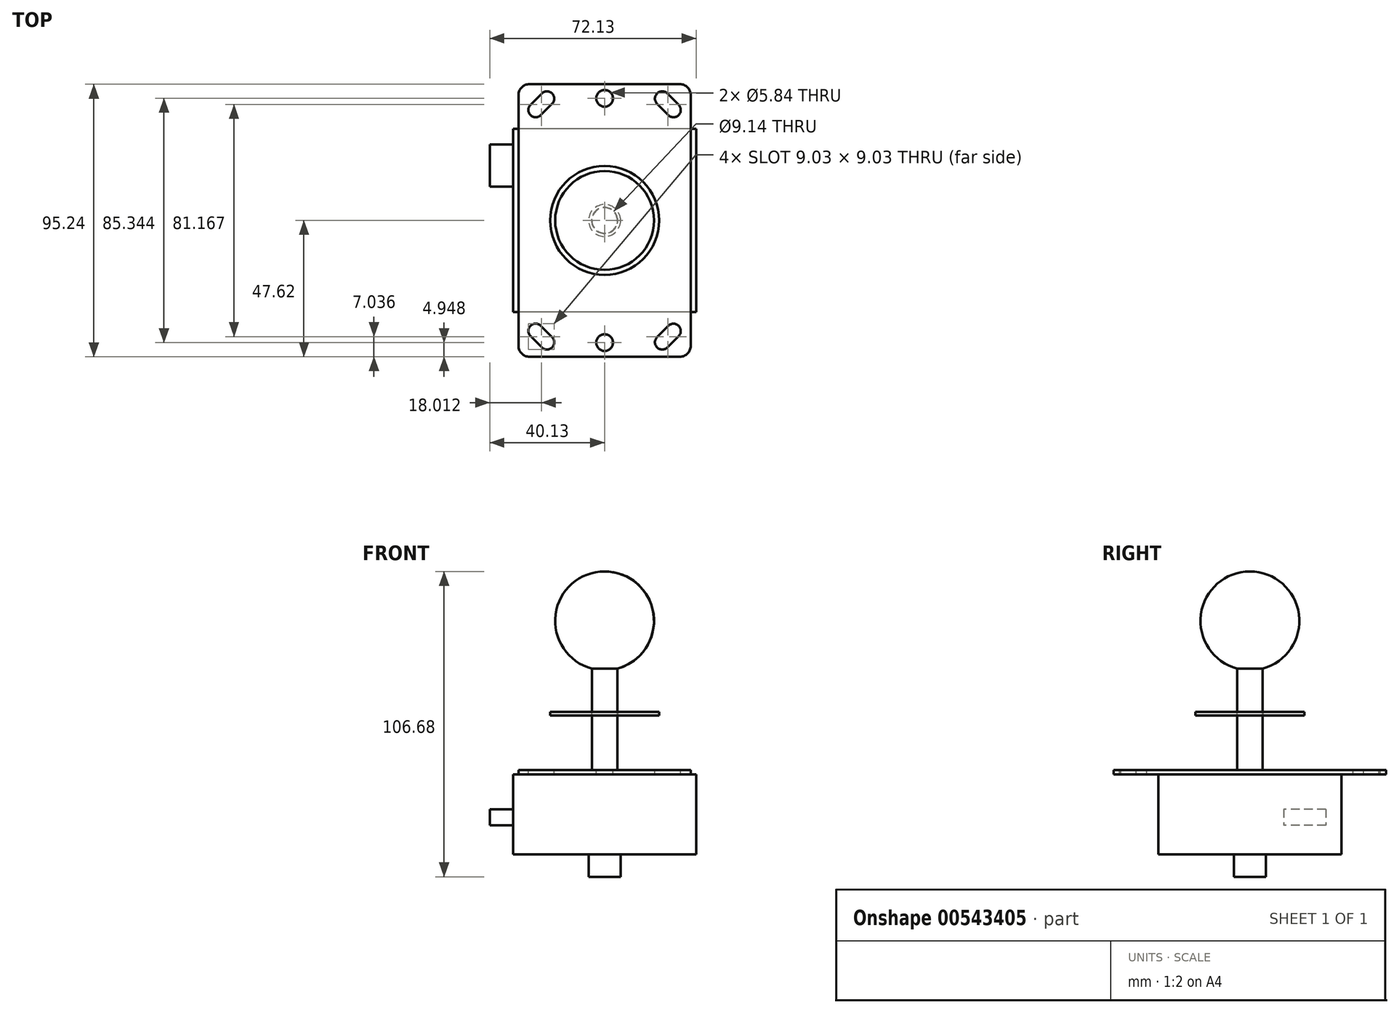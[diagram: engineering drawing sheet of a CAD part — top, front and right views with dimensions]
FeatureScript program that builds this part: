
annotation { "Feature Type Name" : "Feature", "Feature Type Description" : "" }
export const myFeature = defineFeature(function(context is Context, id is Id, definition is map)
    precondition{}
    {
        {
            var Q0;
            Q0=qCreatedBy(makeId("Top.planeOp"),FACE);
            var sketch = newSketch(context, id + "F0", { "sketchPlane" : qUnion([Q0])});
            skLineSegment(sketch, "E0.bottom", {"start": v(-30.1, 47.62) * mm, "end": v(30.1, 47.62) * mm});
            skLineSegment(sketch, "E0.top", {"start": v(-30.1, -47.63) * mm, "end": v(30.1, -47.63) * mm});
            skLineSegment(sketch, "E0.left", {"start": v(-30.1, 47.63) * mm, "end": v(-30.1, -47.63) * mm});
            skLineSegment(sketch, "E0.right", {"start": v(30.1, 47.63) * mm, "end": v(30.1, -47.63) * mm});
            skPoint(sketch, "E0.middle", {"position": v(0, 0) * mm});
            skSolve(sketch);
        }
        {
            var Q0;
            Q0 = qSketchRegion(id + "F0", true);
            extrude(context, id + "F1", {"entities" : qUnion([Q0]), "oppositeDirection" : true, "depth" : 1.52 * mm, "offsetDistance" : 25.4 * mm});
        }
        {
            var Q0;
            Q0=makeQuery(id+"F1.opExtrude","CAP_FACE",FACE,{"disambiguationData":[OSD([sQuery(id+"F0.wireOp",EDGE,"E0.bottom"),sQuery(id+"F0.wireOp",EDGE,"E0.top"),sQuery(id+"F0.wireOp",EDGE,"E0.left"),sQuery(id+"F0.wireOp",EDGE,"E0.right")])],"isStart":false});
            var sketch = newSketch(context, id + "F2", { "sketchPlane" : qUnion([Q0])});
            skLineSegment(sketch, "E1.bottom", {"start": v(32, 32) * mm, "end": v(-32, 32) * mm});
            skLineSegment(sketch, "E1.top", {"start": v(32, -32) * mm, "end": v(-32, -32) * mm});
            skLineSegment(sketch, "E1.left", {"start": v(32, 32) * mm, "end": v(32, -32) * mm});
            skLineSegment(sketch, "E1.right", {"start": v(-32, 32) * mm, "end": v(-32, -32) * mm});
            skPoint(sketch, "E1.middle", {"position": v(0, 0) * mm});
            skSolve(sketch);
        }
        {
            var Q0;
            Q0 = qSketchRegion(id + "F2", true);
            extrude(context, id + "F3", {"entities" : qUnion([Q0]), "operationType" : NewBodyOperationType.ADD, "depth" : 27.94 * mm, "offsetDistance" : 25.4 * mm});
        }
        {
            var Q0;
            {var subQ0=sQuery(id+"F0.wireOp",EDGE,"E0.right");var subQ1=sQuery(id+"F0.wireOp",EDGE,"E0.left");var subQ3=sQuery(id+"F0.wireOp",EDGE,"E0.top");Q0=makeQuery(id+"F3.boolean.opBoolean","SPLIT",FACE,{"disambiguationData":[TD([makeQuery(id+"F1.opExtrude","SWEPT_FACE",FACE,{"disambiguationData":[OSD([subQ3])]})])],"derivedFrom":makeQuery(id+"F1.opExtrude","CAP_FACE",FACE,{"disambiguationData":[OSD([sQuery(id+"F0.wireOp",EDGE,"E0.bottom"),subQ3,subQ1,subQ0])],"isStart":false})});}
            var sketch = newSketch(context, id + "F4", { "sketchPlane" : qUnion([Q0])});
            skCircle(sketch, "E2", {"center": v(0, 0) * mm, "radius": 5.59 * mm});
            skSolve(sketch);
        }
        {
            var Q0;
            Q0 = qSketchRegion(id + "F4", true);
            extrude(context, id + "F5", {"entities" : qUnion([Q0]), "operationType" : NewBodyOperationType.ADD, "depth" : 35.81 * mm, "offsetDistance" : 25.4 * mm});
        }
        {
            var Q0;
            Q0=qCreatedBy(makeId("Front.planeOp"),FACE);
            var sketch = newSketch(context, id + "F6", { "sketchPlane" : qUnion([Q0])});
            skArc(sketch, "E3", {"start": v(0, 69.34) * mm, "mid": v(-17.13, 54.31) * mm, "end": v(-4.45, 35.38) * mm});
            skLineSegment(sketch, "E4", {"start": v(-4.45, 35.38) * mm, "end": v(-4.44, 0) * mm});
            skLineSegment(sketch, "E5", {"start": v(-4.44, 0) * mm, "end": v(0, 0) * mm});
            skLineSegment(sketch, "E6", {"start": v(0, 0) * mm, "end": v(0, 69.34) * mm, "construction": true});
            skArc(sketch, "E7", {"start": v(-4.44, 35.38) * mm, "mid": v(-2.24, 34.94) * mm, "end": v(0, 34.8) * mm, "construction": true});
            skLineSegment(sketch, "E8", {"start": v(0, 69.34) * mm, "end": v(0, 0) * mm});
            skSolve(sketch);
        }
        {
            var Q0;
            Q0 = qSketchRegion(id + "F6", true);
            var Q1;
            Q1=sQuery(id+"F6.wireOp",EDGE,"E8");
            revolve(context, id + "F7", {"operationType" : NewBodyOperationType.ADD, "entities" : qUnion([Q0]), "axis" : qUnion([Q1]), "revolveType" : RevolveType.FULL});
        }
        {
            var Q0;
            Q0=makeQuery(id+"F1.opExtrude","CAP_FACE",FACE,{"disambiguationData":[OSD([sQuery(id+"F0.wireOp",EDGE,"E0.bottom"),sQuery(id+"F0.wireOp",EDGE,"E0.top"),sQuery(id+"F0.wireOp",EDGE,"E0.left"),sQuery(id+"F0.wireOp",EDGE,"E0.right")])],"isStart":true});
            var sketch = newSketch(context, id + "F8", { "sketchPlane" : qUnion([Q0])});
            skLineSegment(sketch, "E9", {"start": v(24.1, -38.6) * mm, "end": v(20.14, -42.56) * mm, "construction": true});
            skArc(sketch, "E10.0.startCap", {"start": v(22.3, -36.81) * mm, "mid": v(25.89, -36.81) * mm, "end": v(25.89, -40.4) * mm});
            skArc(sketch, "E10.0.endCap", {"start": v(21.94, -44.36) * mm, "mid": v(18.35, -44.36) * mm, "end": v(18.35, -40.76) * mm});
            skLineSegment(sketch, "E10.0.left", {"start": v(25.89, -40.4) * mm, "end": v(21.94, -44.36) * mm});
            skLineSegment(sketch, "E10.0.right", {"start": v(22.3, -36.81) * mm, "end": v(18.35, -40.76) * mm});
            skArc(sketch, "E11.0.startCap", {"start": v(22.3, -36.81) * mm, "mid": v(25.89, -36.81) * mm, "end": v(25.89, -40.4) * mm, "construction": true});
            skArc(sketch, "E11.0.endCap", {"start": v(21.94, -44.36) * mm, "mid": v(18.35, -44.36) * mm, "end": v(18.35, -40.76) * mm, "construction": true});
            skLineSegment(sketch, "E11.0.left", {"start": v(25.89, -40.4) * mm, "end": v(21.94, -44.36) * mm, "construction": true});
            skLineSegment(sketch, "E11.0.right", {"start": v(22.3, -36.81) * mm, "end": v(18.35, -40.76) * mm, "construction": true});
            skLineSegment(sketch, "E12.MirrorCS", {"start": v(-22.3, -36.81) * mm, "end": v(-18.35, -40.76) * mm});
            skLineSegment(sketch, "E13.MirrorCS", {"start": v(-25.89, -40.4) * mm, "end": v(-21.94, -44.36) * mm});
            skArc(sketch, "E14.MirrorCS", {"start": v(-22.3, -36.81) * mm, "mid": v(-25.89, -36.81) * mm, "end": v(-25.89, -40.4) * mm});
            skArc(sketch, "E15.MirrorCS", {"start": v(-21.94, -44.36) * mm, "mid": v(-18.35, -44.36) * mm, "end": v(-18.35, -40.76) * mm});
            skLineSegment(sketch, "E16.MirrorCS", {"start": v(-25.89, -40.4) * mm, "end": v(-21.94, -44.36) * mm, "construction": true});
            skArc(sketch, "E17.MirrorCS", {"start": v(-22.3, -36.81) * mm, "mid": v(-25.89, -36.81) * mm, "end": v(-25.89, -40.4) * mm, "construction": true});
            skLineSegment(sketch, "E18.MirrorCS", {"start": v(-24.1, -38.6) * mm, "end": v(-20.14, -42.56) * mm, "construction": true});
            skLineSegment(sketch, "E19.MirrorCS", {"start": v(-22.3, -36.81) * mm, "end": v(-18.35, -40.76) * mm, "construction": true});
            skArc(sketch, "E20.MirrorCS", {"start": v(-21.94, -44.36) * mm, "mid": v(-18.35, -44.36) * mm, "end": v(-18.35, -40.76) * mm, "construction": true});
            skArc(sketch, "E21.MirrorCS", {"start": v(-21.94, 44.36) * mm, "mid": v(-18.35, 44.36) * mm, "end": v(-18.35, 40.76) * mm});
            skLineSegment(sketch, "E22.MirrorCS", {"start": v(-22.3, 36.81) * mm, "end": v(-18.35, 40.76) * mm});
            skLineSegment(sketch, "E23.MirrorCS", {"start": v(-25.89, 40.4) * mm, "end": v(-21.94, 44.36) * mm});
            skArc(sketch, "E24.MirrorCS", {"start": v(-22.3, 36.81) * mm, "mid": v(-25.89, 36.81) * mm, "end": v(-25.89, 40.4) * mm});
            skArc(sketch, "E25.MirrorCS", {"start": v(21.94, 44.36) * mm, "mid": v(18.35, 44.36) * mm, "end": v(18.35, 40.76) * mm});
            skLineSegment(sketch, "E26.MirrorCS", {"start": v(-25.89, 40.4) * mm, "end": v(-21.94, 44.36) * mm, "construction": true});
            skArc(sketch, "E27.MirrorCS", {"start": v(22.3, 36.81) * mm, "mid": v(25.89, 36.81) * mm, "end": v(25.89, 40.4) * mm});
            skLineSegment(sketch, "E28.MirrorCS", {"start": v(-22.3, 36.81) * mm, "end": v(-18.35, 40.76) * mm, "construction": true});
            skLineSegment(sketch, "E29.MirrorCS", {"start": v(25.89, 40.4) * mm, "end": v(21.94, 44.36) * mm});
            skLineSegment(sketch, "E30.MirrorCS", {"start": v(-24.1, 38.6) * mm, "end": v(-20.14, 42.56) * mm, "construction": true});
            skArc(sketch, "E31.MirrorCS", {"start": v(-21.94, 44.36) * mm, "mid": v(-18.35, 44.36) * mm, "end": v(-18.35, 40.76) * mm, "construction": true});
            skArc(sketch, "E32.MirrorCS", {"start": v(-22.3, 36.81) * mm, "mid": v(-25.89, 36.81) * mm, "end": v(-25.89, 40.4) * mm, "construction": true});
            skLineSegment(sketch, "E33.MirrorCS", {"start": v(22.3, 36.81) * mm, "end": v(18.35, 40.76) * mm});
            skLineSegment(sketch, "E34.MirrorCS", {"start": v(25.89, 40.4) * mm, "end": v(21.94, 44.36) * mm, "construction": true});
            skLineSegment(sketch, "E35.MirrorCS", {"start": v(24.1, 38.6) * mm, "end": v(20.14, 42.56) * mm, "construction": true});
            skLineSegment(sketch, "E36.MirrorCS", {"start": v(22.3, 36.81) * mm, "end": v(18.35, 40.76) * mm, "construction": true});
            skArc(sketch, "E37.MirrorCS", {"start": v(21.94, 44.36) * mm, "mid": v(18.35, 44.36) * mm, "end": v(18.35, 40.76) * mm, "construction": true});
            skArc(sketch, "E38.MirrorCS", {"start": v(22.3, 36.81) * mm, "mid": v(25.89, 36.81) * mm, "end": v(25.89, 40.4) * mm, "construction": true});
            skCircle(sketch, "E39", {"center": v(0, -42.67) * mm, "radius": 2.92 * mm});
            skCircle(sketch, "E40.MirrorC", {"center": v(0, 42.67) * mm, "radius": 2.92 * mm});
            skSolve(sketch);
        }
        {
            var Q0;
            Q0 = qSketchRegion(id + "F8", true);
            extrude(context, id + "F9", {"entities" : qUnion([Q0]), "operationType" : NewBodyOperationType.REMOVE, "endBound" : BoundingType.THROUGH_ALL, "oppositeDirection" : true, "depth" : 25.4 * mm, "offsetDistance" : 25.4 * mm});
        }
        {
            var Q0;
            Q0=makeQuery(id+"F1.opExtrude","SWEPT_EDGE",EDGE,{"disambiguationData":[OSD([sQuery(id+"F0.wireOp",EDGE,"E0.top"),sQuery(id+"F0.wireOp",EDGE,"E0.right")])]});
            var Q1;
            Q1=makeQuery(id+"F1.opExtrude","SWEPT_EDGE",EDGE,{"disambiguationData":[OSD([sQuery(id+"F0.wireOp",EDGE,"E0.top"),sQuery(id+"F0.wireOp",EDGE,"E0.left")])]});
            var Q2;
            Q2=makeQuery(id+"F1.opExtrude","SWEPT_EDGE",EDGE,{"disambiguationData":[OSD([sQuery(id+"F0.wireOp",EDGE,"E0.bottom"),sQuery(id+"F0.wireOp",EDGE,"E0.left")])]});
            var Q3;
            Q3=makeQuery(id+"F1.opExtrude","SWEPT_EDGE",EDGE,{"disambiguationData":[OSD([sQuery(id+"F0.wireOp",EDGE,"E0.bottom"),sQuery(id+"F0.wireOp",EDGE,"E0.right")])]});
            fillet(context, id + "F10", {"entities" : qUnion([Q0, Q1, Q2, Q3]), "radius" : 3.8 * mm, "tangentPropagation" : true, "allowEdgeOverflow" : false});
        }
        {
            var Q0;
            Q0=makeQuery(id+"F1.opExtrude","CAP_FACE",FACE,{"disambiguationData":[OSD([sQuery(id+"F0.wireOp",EDGE,"E0.bottom"),sQuery(id+"F0.wireOp",EDGE,"E0.top"),sQuery(id+"F0.wireOp",EDGE,"E0.left"),sQuery(id+"F0.wireOp",EDGE,"E0.right")])],"isStart":true});
            cPlane(context, id + "F11", {"entities" : qUnion([Q0]), "cplaneType" : CPlaneType.OFFSET, "offset" : 19.05 * mm, "width" : 152.4 * mm, "height" : 152.4 * mm});
        }
        {
            var Q0;
            Q0=qCreatedBy(id+"F11.planeOp",FACE);
            var sketch = newSketch(context, id + "F12", { "sketchPlane" : qUnion([Q0])});
            skCircle(sketch, "E41", {"center": v(0, 0) * mm, "radius": 19.05 * mm});
            skCircle(sketch, "E42", {"center": v(0, 0) * mm, "radius": 4.57 * mm});
            skSolve(sketch);
        }
        {
            var Q0;
            Q0 = qSketchRegion(id + "F12", true);
            extrude(context, id + "F13", {"entities" : qUnion([Q0]), "operationType" : NewBodyOperationType.ADD, "depth" : 1.27 * mm, "offsetDistance" : 25.4 * mm});
        }
        {
            var Q0;
            Q0=makeQuery(id+"F3.opExtrude","SWEPT_FACE",FACE,{"disambiguationData":[OSD([sQuery(id+"F2.wireOp",EDGE,"E1.right")])]});
            var sketch = newSketch(context, id + "F14", { "sketchPlane" : qUnion([Q0])});
            skLineSegment(sketch, "E43.bottom", {"start": v(-26.54, -13.72) * mm, "end": v(-11.81, -13.72) * mm});
            skLineSegment(sketch, "E43.top", {"start": v(-26.54, -19.3) * mm, "end": v(-11.81, -19.3) * mm});
            skLineSegment(sketch, "E43.left", {"start": v(-26.54, -13.72) * mm, "end": v(-26.54, -19.3) * mm});
            skLineSegment(sketch, "E43.right", {"start": v(-11.81, -13.72) * mm, "end": v(-11.81, -19.3) * mm});
            skPoint(sketch, "E43.middle", {"position": v(-19.18, -16.51) * mm});
            skSolve(sketch);
        }
        {
            var Q0;
            Q0 = qSketchRegion(id + "F14", true);
            extrude(context, id + "F15", {"entities" : qUnion([Q0]), "operationType" : NewBodyOperationType.ADD, "depth" : 8.13 * mm, "offsetDistance" : 25.4 * mm});
        }
    });
